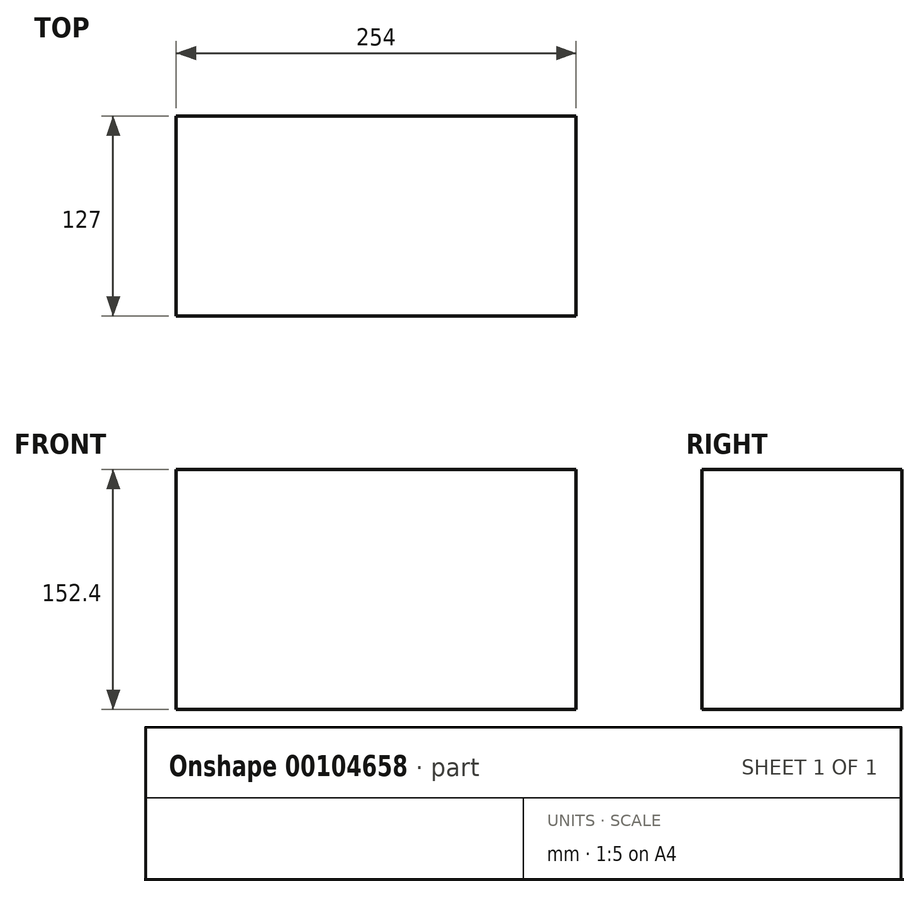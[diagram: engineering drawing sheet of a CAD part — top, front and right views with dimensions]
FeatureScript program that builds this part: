
annotation { "Feature Type Name" : "Feature", "Feature Type Description" : "" }
export const myFeature = defineFeature(function(context is Context, id is Id, definition is map)
    precondition{}
    {
        {
            var Q0;
            Q0=qCreatedBy(makeId("Front.planeOp"),FACE);
            var sketch = newSketch(context, id + "F0", { "sketchPlane" : qUnion([Q0])});
            skLineSegment(sketch, "E0", {"start": v(0, 0) * mm, "end": v(0, 152.4) * mm});
            skLineSegment(sketch, "E1", {"start": v(0, 152.4) * mm, "end": v(254, 152.4) * mm});
            skLineSegment(sketch, "E2", {"start": v(254, 152.4) * mm, "end": v(254, 0) * mm});
            skLineSegment(sketch, "E3", {"start": v(254, 0) * mm, "end": v(0, 0) * mm});
            skSolve(sketch);
        }
        {
            var Q0;
            Q0 = qSketchRegion(id + "F0", true);
            extrude(context, id + "F1", {"entities" : qUnion([Q0]), "depth" : 127 * mm});
        }
    });
